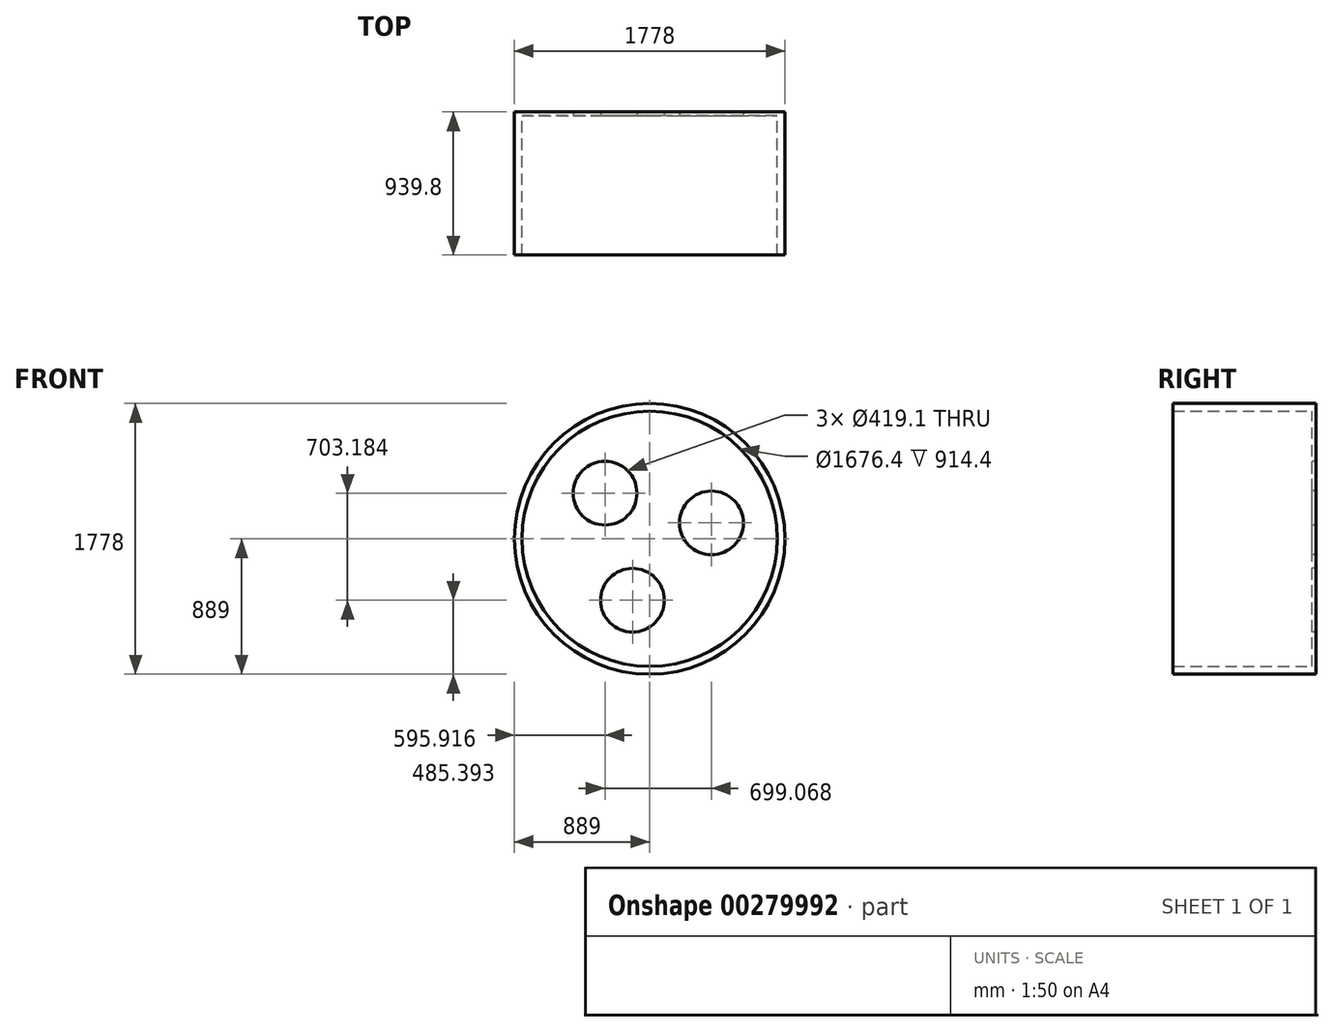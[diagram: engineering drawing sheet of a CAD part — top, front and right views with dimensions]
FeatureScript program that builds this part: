
annotation { "Feature Type Name" : "Feature", "Feature Type Description" : "" }
export const myFeature = defineFeature(function(context is Context, id is Id, definition is map)
    precondition{}
    {
        {
            var Q0;
            Q0=qCreatedBy(makeId("Front.planeOp"),FACE);
            var sketch = newSketch(context, id + "F0", { "sketchPlane" : qUnion([Q0])});
            skCircle(sketch, "E0", {"center": v(0, 0) * mm, "radius": 889 * mm});
            skCircle(sketch, "E1", {"center": v(0, 0) * mm, "radius": 838.2 * mm});
            skLineSegment(sketch, "E2", {"start": v(0, 0) * mm, "end": v(-586.17, 599.15) * mm});
            skPoint(sketch, "E3", {"position": v(-293.08, 299.58) * mm});
            skLineSegment(sketch, "E4", {"start": v(-586.17, 599.15) * mm, "end": v(-293.08, 299.58) * mm});
            skPoint(sketch, "E5", {"position": v(-439.63, 449.37) * mm});
            skCircle(sketch, "E6", {"center": v(-293.08, 299.58) * mm, "radius": 209.55 * mm});
            skCircle(sketch, "E7.1.0", {"center": v(-112.9, -403.6) * mm, "radius": 209.55 * mm});
            skCircle(sketch, "E7.2.0", {"center": v(405.98, 104.03) * mm, "radius": 209.55 * mm});
            skSolve(sketch);
        }
        {
            var Q0;
            Q0=makeQuery(id+"F0.imprint","IMPRINT",FACE,{"disambiguationData":[TD([[makeQuery(id+"F0.imprint","IMPRINT",EDGE,{"derivedFrom":sQuery(id+"F0.wireOp",EDGE,"E0")}),1.0]])]});
            extrude(context, id + "F1", {"entities" : qUnion([Q0]), "depth" : 914.4 * mm});
        }
        {
            var Q0;
            Q0=makeQuery(id+"F0.imprint","IMPRINT",FACE,{"disambiguationData":[TD([[makeQuery(id+"F0.imprint","IMPRINT",EDGE,{"derivedFrom":sQuery(id+"F0.wireOp",EDGE,"E1")}),1.0]])]});
            var Q1;
            Q1=makeQuery(id+"F0.imprint","IMPRINT",FACE,{"disambiguationData":[TD([[makeQuery(id+"F0.imprint","IMPRINT",EDGE,{"derivedFrom":sQuery(id+"F0.wireOp",EDGE,"E0")}),1.0]])]});
            extrude(context, id + "F2", {"entities" : qUnion([Q0, Q1]), "operationType" : NewBodyOperationType.ADD, "oppositeDirection" : true, "depth" : 25.4 * mm});
        }
    });
